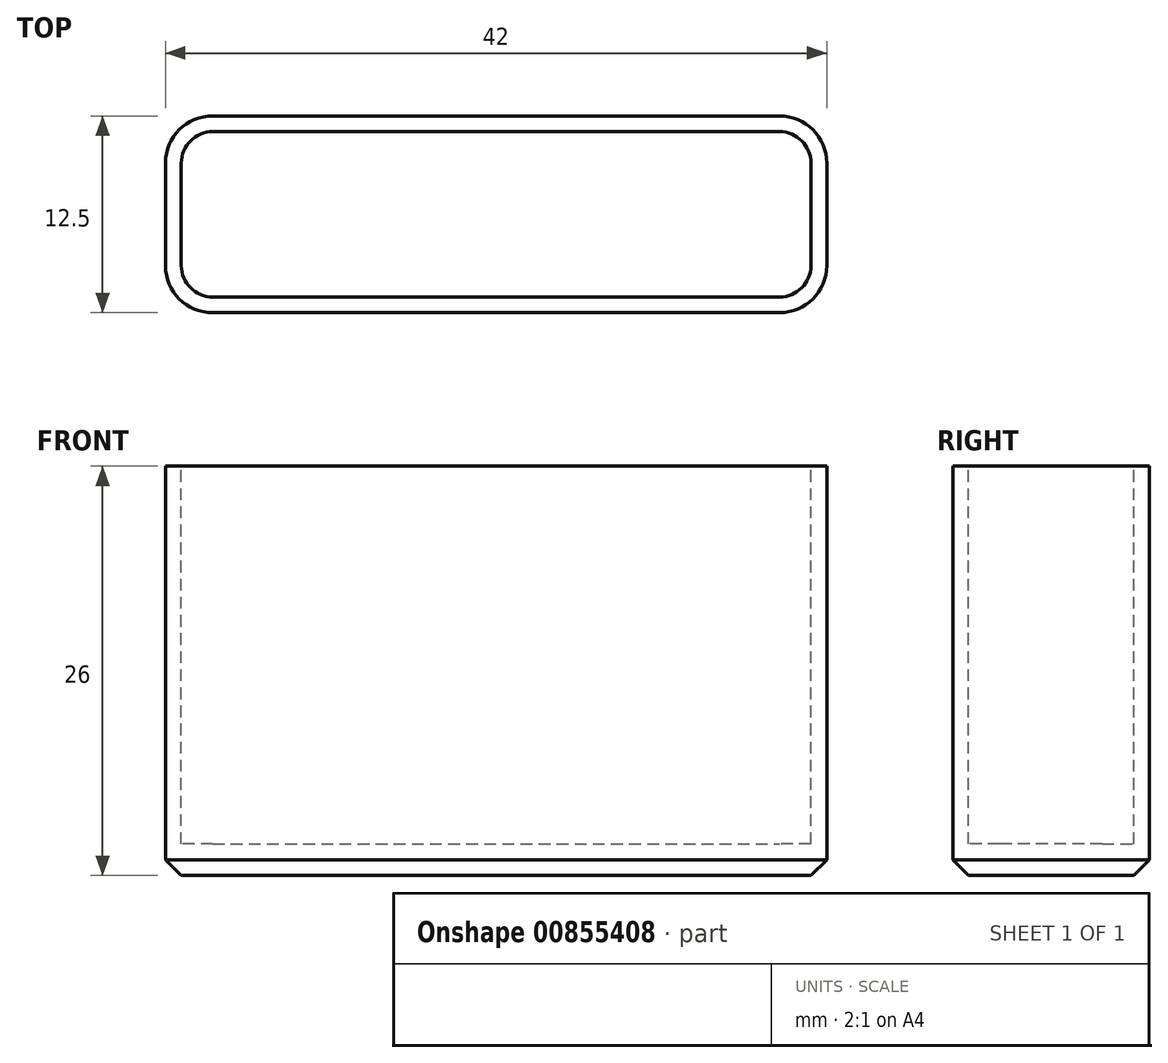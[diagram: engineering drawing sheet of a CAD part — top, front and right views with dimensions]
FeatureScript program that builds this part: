
annotation { "Feature Type Name" : "Feature", "Feature Type Description" : "" }
export const myFeature = defineFeature(function(context is Context, id is Id, definition is map)
    precondition{}
    {
        {
            var Q0;
            Q0=qCreatedBy(makeId("Top.planeOp"),FACE);
            var sketch = newSketch(context, id + "F0", { "sketchPlane" : qUnion([Q0])});
            skLineSegment(sketch, "E0.bottom", {"start": v(-21, 6.25) * mm, "end": v(21, 6.25) * mm});
            skLineSegment(sketch, "E0.top", {"start": v(-21, -6.25) * mm, "end": v(21, -6.25) * mm});
            skLineSegment(sketch, "E0.left", {"start": v(-21, 6.25) * mm, "end": v(-21, -6.25) * mm});
            skLineSegment(sketch, "E0.right", {"start": v(21, 6.25) * mm, "end": v(21, -6.25) * mm});
            skSolve(sketch);
        }
        {
            var Q0;
            Q0 = qSketchRegion(id + "F0", true);
            extrude(context, id + "F1", {"entities" : qUnion([Q0]), "depth" : 26 * mm, "offsetDistance" : 25 * mm});
        }
        {
            var Q0;
            Q0=makeQuery(id+"F1.opExtrude","SWEPT_EDGE",EDGE,{"disambiguationData":[OSD([sQuery(id+"F0.wireOp",EDGE,"E0.bottom"),sQuery(id+"F0.wireOp",EDGE,"E0.left")])]});
            var Q1;
            Q1=makeQuery(id+"F1.opExtrude","SWEPT_EDGE",EDGE,{"disambiguationData":[OSD([sQuery(id+"F0.wireOp",EDGE,"E0.top"),sQuery(id+"F0.wireOp",EDGE,"E0.left")])]});
            var Q2;
            Q2=makeQuery(id+"F1.opExtrude","SWEPT_EDGE",EDGE,{"disambiguationData":[OSD([sQuery(id+"F0.wireOp",EDGE,"E0.bottom"),sQuery(id+"F0.wireOp",EDGE,"E0.right")])]});
            var Q3;
            Q3=makeQuery(id+"F1.opExtrude","SWEPT_EDGE",EDGE,{"disambiguationData":[OSD([sQuery(id+"F0.wireOp",EDGE,"E0.top"),sQuery(id+"F0.wireOp",EDGE,"E0.right")])]});
            fillet(context, id + "F2", {"entities" : qUnion([Q0, Q1, Q2, Q3]), "radius" : 3 * mm, "tangentPropagation" : true, "allowEdgeOverflow" : false});
        }
        {
            var Q0;
            Q0=makeQuery(id+"F1.opExtrude","CAP_FACE",FACE,{"disambiguationData":[OSD([sQuery(id+"F0.wireOp",EDGE,"E0.bottom"),sQuery(id+"F0.wireOp",EDGE,"E0.top"),sQuery(id+"F0.wireOp",EDGE,"E0.left"),sQuery(id+"F0.wireOp",EDGE,"E0.right")])],"isStart":false});
            var sketch = newSketch(context, id + "F3", { "sketchPlane" : qUnion([Q0])});
            skLineSegment(sketch, "E1.bottom", {"start": v(-18, 5.25) * mm, "end": v(18, 5.25) * mm});
            skLineSegment(sketch, "E1.top", {"start": v(-18, -5.25) * mm, "end": v(18, -5.25) * mm});
            skLineSegment(sketch, "E1.left", {"start": v(-20, 3.25) * mm, "end": v(-20, -3.25) * mm});
            skLineSegment(sketch, "E1.right", {"start": v(20, 3.25) * mm, "end": v(20, -3.25) * mm});
            skPoint(sketch, "E2.visualSharp", {"position": v(-20, 5.25) * mm});
            skArc(sketch, "E2.filletArc", {"start": v(-18, 5.25) * mm, "mid": v(-19.41, 4.66) * mm, "end": v(-20, 3.25) * mm});
            skPoint(sketch, "E3.visualSharp", {"position": v(20, 5.25) * mm});
            skArc(sketch, "E3.filletArc", {"start": v(20, 3.25) * mm, "mid": v(19.41, 4.66) * mm, "end": v(18, 5.25) * mm});
            skPoint(sketch, "E4.visualSharp", {"position": v(20, -5.25) * mm});
            skArc(sketch, "E4.filletArc", {"start": v(18, -5.25) * mm, "mid": v(19.41, -4.66) * mm, "end": v(20, -3.25) * mm});
            skPoint(sketch, "E5.visualSharp", {"position": v(-20, -5.25) * mm});
            skArc(sketch, "E5.filletArc", {"start": v(-20, -3.25) * mm, "mid": v(-19.41, -4.66) * mm, "end": v(-18, -5.25) * mm});
            skSolve(sketch);
        }
        {
            var Q0;
            Q0 = qSketchRegion(id + "F3", true);
            extrude(context, id + "F4", {"entities" : qUnion([Q0]), "operationType" : NewBodyOperationType.REMOVE, "oppositeDirection" : true, "depth" : 24 * mm, "offsetDistance" : 25 * mm});
        }
        {
            var Q0;
            Q0=makeQuery(id+"F1.opExtrude","CAP_EDGE",EDGE,{"disambiguationData":[OSD([sQuery(id+"F0.wireOp",EDGE,"E0.bottom")])],"isStart":true});
            var Q1;
            {var subQ0=sQuery(id+"F0.wireOp",EDGE,"E0.right");var subQ1=sQuery(id+"F0.wireOp",EDGE,"E0.bottom");Q1=makeQuery(id+"F2.opFillet","BLEND_EDGE",EDGE,{"blendedFrom":[makeQuery(id+"F1.opExtrude","SWEPT_EDGE",EDGE,{"disambiguationData":[OSD([subQ1,subQ0])]}),makeQuery(id+"F1.opExtrude","CAP_FACE",FACE,{"disambiguationData":[OSD([subQ1,sQuery(id+"F0.wireOp",EDGE,"E0.top"),sQuery(id+"F0.wireOp",EDGE,"E0.left"),subQ0])],"isStart":true})],"blendedInto":[makeQuery(id+"F1.opExtrude","CAP_FACE",FACE,{"disambiguationData":[OSD([subQ1,sQuery(id+"F0.wireOp",EDGE,"E0.top"),sQuery(id+"F0.wireOp",EDGE,"E0.left"),subQ0])],"isStart":true})]});}
            var Q2;
            Q2=makeQuery(id+"F1.opExtrude","CAP_EDGE",EDGE,{"disambiguationData":[OSD([sQuery(id+"F0.wireOp",EDGE,"E0.right")])],"isStart":true});
            var Q3;
            {var subQ0=sQuery(id+"F0.wireOp",EDGE,"E0.right");var subQ1=sQuery(id+"F0.wireOp",EDGE,"E0.top");Q3=makeQuery(id+"F2.opFillet","BLEND_EDGE",EDGE,{"blendedFrom":[makeQuery(id+"F1.opExtrude","SWEPT_EDGE",EDGE,{"disambiguationData":[OSD([subQ1,subQ0])]}),makeQuery(id+"F1.opExtrude","CAP_FACE",FACE,{"disambiguationData":[OSD([sQuery(id+"F0.wireOp",EDGE,"E0.bottom"),subQ1,sQuery(id+"F0.wireOp",EDGE,"E0.left"),subQ0])],"isStart":true})],"blendedInto":[makeQuery(id+"F1.opExtrude","CAP_FACE",FACE,{"disambiguationData":[OSD([sQuery(id+"F0.wireOp",EDGE,"E0.bottom"),subQ1,sQuery(id+"F0.wireOp",EDGE,"E0.left"),subQ0])],"isStart":true})]});}
            var Q4;
            Q4=makeQuery(id+"F1.opExtrude","CAP_EDGE",EDGE,{"disambiguationData":[OSD([sQuery(id+"F0.wireOp",EDGE,"E0.top")])],"isStart":true});
            var Q5;
            {var subQ0=sQuery(id+"F0.wireOp",EDGE,"E0.left");var subQ1=sQuery(id+"F0.wireOp",EDGE,"E0.top");Q5=makeQuery(id+"F2.opFillet","BLEND_EDGE",EDGE,{"blendedFrom":[makeQuery(id+"F1.opExtrude","SWEPT_EDGE",EDGE,{"disambiguationData":[OSD([subQ1,subQ0])]}),makeQuery(id+"F1.opExtrude","CAP_FACE",FACE,{"disambiguationData":[OSD([sQuery(id+"F0.wireOp",EDGE,"E0.bottom"),subQ1,subQ0,sQuery(id+"F0.wireOp",EDGE,"E0.right")])],"isStart":true})],"blendedInto":[makeQuery(id+"F1.opExtrude","CAP_FACE",FACE,{"disambiguationData":[OSD([sQuery(id+"F0.wireOp",EDGE,"E0.bottom"),subQ1,subQ0,sQuery(id+"F0.wireOp",EDGE,"E0.right")])],"isStart":true})]});}
            var Q6;
            Q6=makeQuery(id+"F1.opExtrude","CAP_EDGE",EDGE,{"disambiguationData":[OSD([sQuery(id+"F0.wireOp",EDGE,"E0.left")])],"isStart":true});
            var Q7;
            {var subQ0=sQuery(id+"F0.wireOp",EDGE,"E0.left");var subQ1=sQuery(id+"F0.wireOp",EDGE,"E0.bottom");Q7=makeQuery(id+"F2.opFillet","BLEND_EDGE",EDGE,{"blendedFrom":[makeQuery(id+"F1.opExtrude","SWEPT_EDGE",EDGE,{"disambiguationData":[OSD([subQ1,subQ0])]}),makeQuery(id+"F1.opExtrude","CAP_FACE",FACE,{"disambiguationData":[OSD([subQ1,sQuery(id+"F0.wireOp",EDGE,"E0.top"),subQ0,sQuery(id+"F0.wireOp",EDGE,"E0.right")])],"isStart":true})],"blendedInto":[makeQuery(id+"F1.opExtrude","CAP_FACE",FACE,{"disambiguationData":[OSD([subQ1,sQuery(id+"F0.wireOp",EDGE,"E0.top"),subQ0,sQuery(id+"F0.wireOp",EDGE,"E0.right")])],"isStart":true})]});}
            chamfer(context, id + "F5", {"entities" : qUnion([Q0, Q1, Q2, Q3, Q4, Q5, Q6, Q7]), "width" : 1 * mm, "tangentPropagation" : true});
        }
    });
